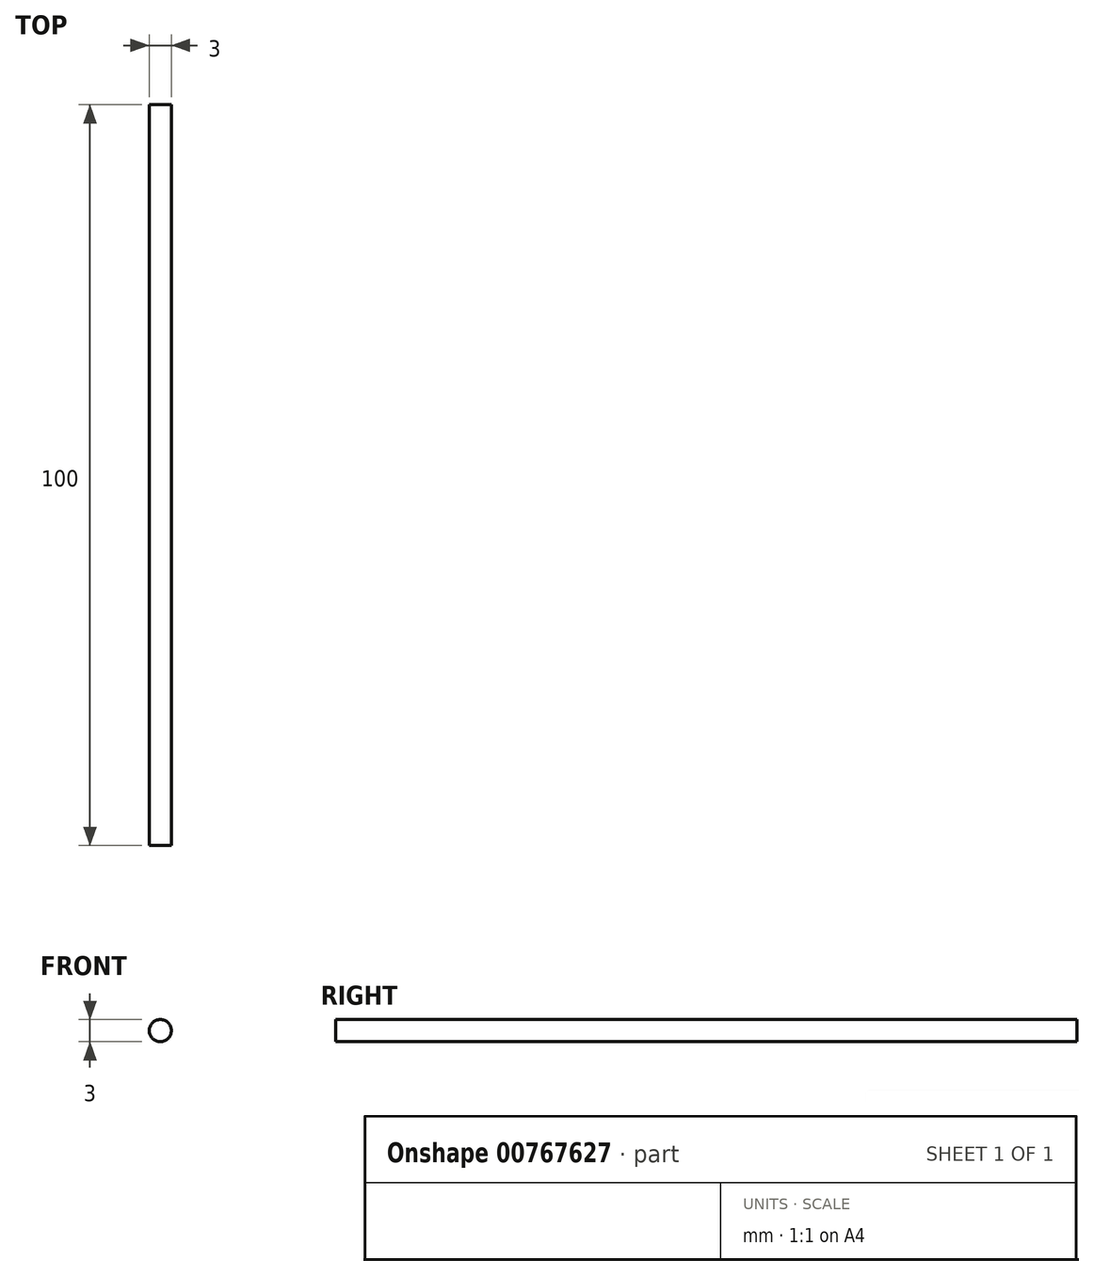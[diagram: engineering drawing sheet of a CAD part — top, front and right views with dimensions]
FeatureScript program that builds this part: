
annotation { "Feature Type Name" : "Feature", "Feature Type Description" : "" }
export const myFeature = defineFeature(function(context is Context, id is Id, definition is map)
    precondition{}
    {
        {
            var Q0;
            Q0=qCreatedBy(makeId("Front.planeOp"),FACE);
            var sketch = newSketch(context, id + "F0", { "sketchPlane" : qUnion([Q0])});
            skCircle(sketch, "E0", {"center": v(0, 0) * mm, "radius": 1.5 * mm});
            skSolve(sketch);
        }
        {
            var Q0;
            Q0=makeQuery(id+"F0.imprint","IMPRINT",FACE,{"disambiguationData":[TD([[makeQuery(id+"F0.imprint","IMPRINT",EDGE,{"derivedFrom":sQuery(id+"F0.wireOp",EDGE,"E0")}),1.0]])]});
            extrude(context, id + "F1", {"entities" : qUnion([Q0]), "endBound" : BoundingType.SYMMETRIC, "depth" : 100 * mm, "offsetDistance" : 25 * mm});
        }
    });
